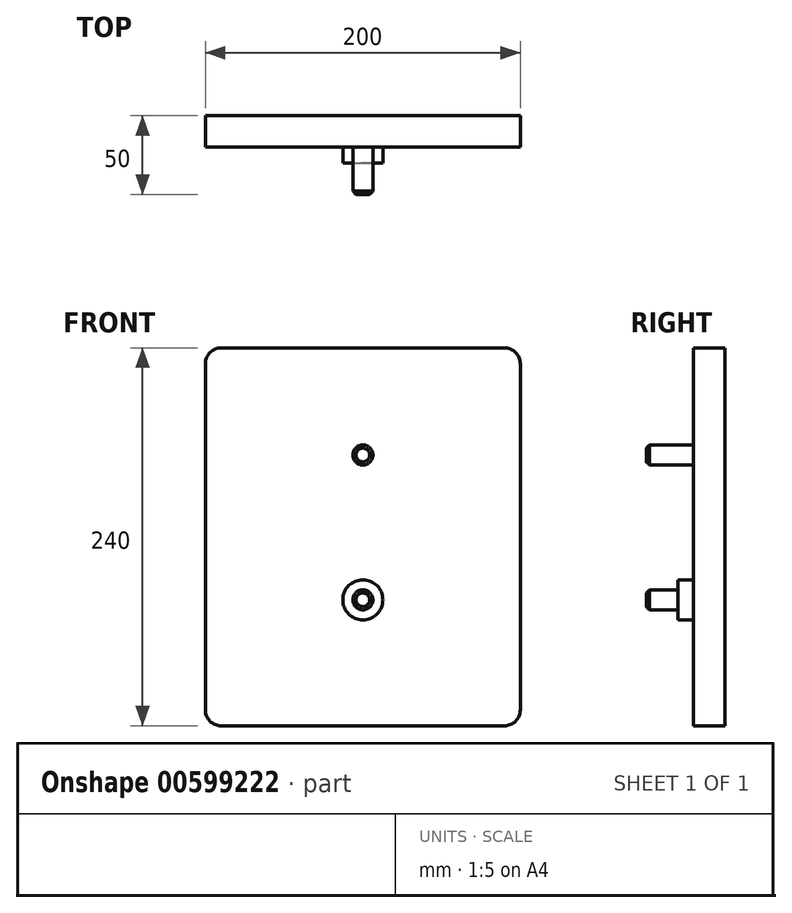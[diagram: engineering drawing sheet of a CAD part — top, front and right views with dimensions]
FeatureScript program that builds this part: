
annotation { "Feature Type Name" : "Feature", "Feature Type Description" : "" }
export const myFeature = defineFeature(function(context is Context, id is Id, definition is map)
    precondition{}
    {
        {
            var Q0;
            Q0=qCreatedBy(makeId("Front.planeOp"),FACE);
            var sketch = newSketch(context, id + "F0", { "sketchPlane" : qUnion([Q0])});
            skCircle(sketch, "E0", {"center": v(0, 92) * mm, "radius": 6.35 * mm, "construction": true});
            skCircle(sketch, "E1", {"center": v(0, 92) * mm, "radius": 31.75 * mm, "construction": true});
            skCircle(sketch, "E2", {"center": v(0, 0) * mm, "radius": 73 * mm, "construction": true});
            skLineSegment(sketch, "E3", {"start": v(0, 0) * mm, "end": v(36.5, 63.22) * mm, "construction": true});
            skCircle(sketch, "E4", {"center": v(0, 38.5) * mm, "radius": 6.35 * mm, "construction": true});
            skSolve(sketch);
        }
        {
            var Q0;
            Q0=qCreatedBy(makeId("Front.planeOp"),FACE);
            var sketch = newSketch(context, id + "F1", { "sketchPlane" : qUnion([Q0])});
            skLineSegment(sketch, "E5.bottom", {"start": v(-100, 160) * mm, "end": v(100, 160) * mm});
            skLineSegment(sketch, "E5.top", {"start": v(-100, -80) * mm, "end": v(100, -80) * mm});
            skLineSegment(sketch, "E5.left", {"start": v(-100, 160) * mm, "end": v(-100, -80) * mm});
            skLineSegment(sketch, "E5.right", {"start": v(100, 160) * mm, "end": v(100, -80) * mm});
            skSolve(sketch);
        }
        {
            var Q0;
            Q0 = qSketchRegion(id + "F1", true);
            extrude(context, id + "F2", {"entities" : qUnion([Q0]), "oppositeDirection" : true, "depth" : 20 * mm, "offsetDistance" : 25 * mm});
        }
        {
            var Q0;
            Q0=qCreatedBy(makeId("Front.planeOp"),FACE);
            var sketch = newSketch(context, id + "F3", { "sketchPlane" : qUnion([Q0])});
            skCircle(sketch, "E6", {"center": v(0, 92) * mm, "radius": 6.35 * mm});
            skCircle(sketch, "E7", {"center": v(0, 0) * mm, "radius": 6.35 * mm});
            skSolve(sketch);
        }
        {
            var Q0;
            Q0 = qSketchRegion(id + "F3", true);
            extrude(context, id + "F4", {"entities" : qUnion([Q0]), "operationType" : NewBodyOperationType.ADD, "depth" : 30 * mm, "offsetDistance" : 25 * mm});
        }
        {
            var Q0;
            Q0=makeQuery(id+"F4.opExtrude","CAP_EDGE",EDGE,{"disambiguationData":[OSD([sQuery(id+"F3.wireOp",EDGE,"E6")])],"isStart":false});
            var Q1;
            Q1=makeQuery(id+"F4.opExtrude","CAP_EDGE",EDGE,{"disambiguationData":[OSD([sQuery(id+"F3.wireOp",EDGE,"E7")])],"isStart":false});
            chamfer(context, id + "F5", {"entities" : qUnion([Q0, Q1]), "width" : 2 * mm, "tangentPropagation" : true});
        }
        {
            var Q0;
            Q0=makeQuery(id+"F2.opExtrude","SWEPT_EDGE",EDGE,{"disambiguationData":[OSD([sQuery(id+"F1.wireOp",EDGE,"E5.bottom"),sQuery(id+"F1.wireOp",EDGE,"E5.left")])]});
            var Q1;
            Q1=makeQuery(id+"F2.opExtrude","SWEPT_EDGE",EDGE,{"disambiguationData":[OSD([sQuery(id+"F1.wireOp",EDGE,"E5.top"),sQuery(id+"F1.wireOp",EDGE,"E5.left")])]});
            var Q2;
            Q2=makeQuery(id+"F2.opExtrude","SWEPT_EDGE",EDGE,{"disambiguationData":[OSD([sQuery(id+"F1.wireOp",EDGE,"E5.top"),sQuery(id+"F1.wireOp",EDGE,"E5.right")])]});
            var Q3;
            Q3=makeQuery(id+"F2.opExtrude","SWEPT_EDGE",EDGE,{"disambiguationData":[OSD([sQuery(id+"F1.wireOp",EDGE,"E5.bottom"),sQuery(id+"F1.wireOp",EDGE,"E5.right")])]});
            fillet(context, id + "F6", {"entities" : qUnion([Q0, Q1, Q2, Q3]), "radius" : 10 * mm, "tangentPropagation" : true, "allowEdgeOverflow" : false});
        }
        {
            var Q0;
            Q0=makeQuery(id+"F2.opExtrude","CAP_FACE",FACE,{"disambiguationData":[OSD([sQuery(id+"F1.wireOp",EDGE,"E5.bottom"),sQuery(id+"F1.wireOp",EDGE,"E5.top"),sQuery(id+"F1.wireOp",EDGE,"E5.left"),sQuery(id+"F1.wireOp",EDGE,"E5.right")])],"isStart":true});
            var sketch = newSketch(context, id + "F7", { "sketchPlane" : qUnion([Q0])});
            skCircle(sketch, "E8", {"center": v(0, 0) * mm, "radius": 12.7 * mm});
            skSolve(sketch);
        }
        {
            var Q0;
            Q0 = qSketchRegion(id + "F7", true);
            extrude(context, id + "F8", {"entities" : qUnion([Q0]), "operationType" : NewBodyOperationType.ADD, "depth" : 10 * mm, "offsetDistance" : 25 * mm});
        }
    });
